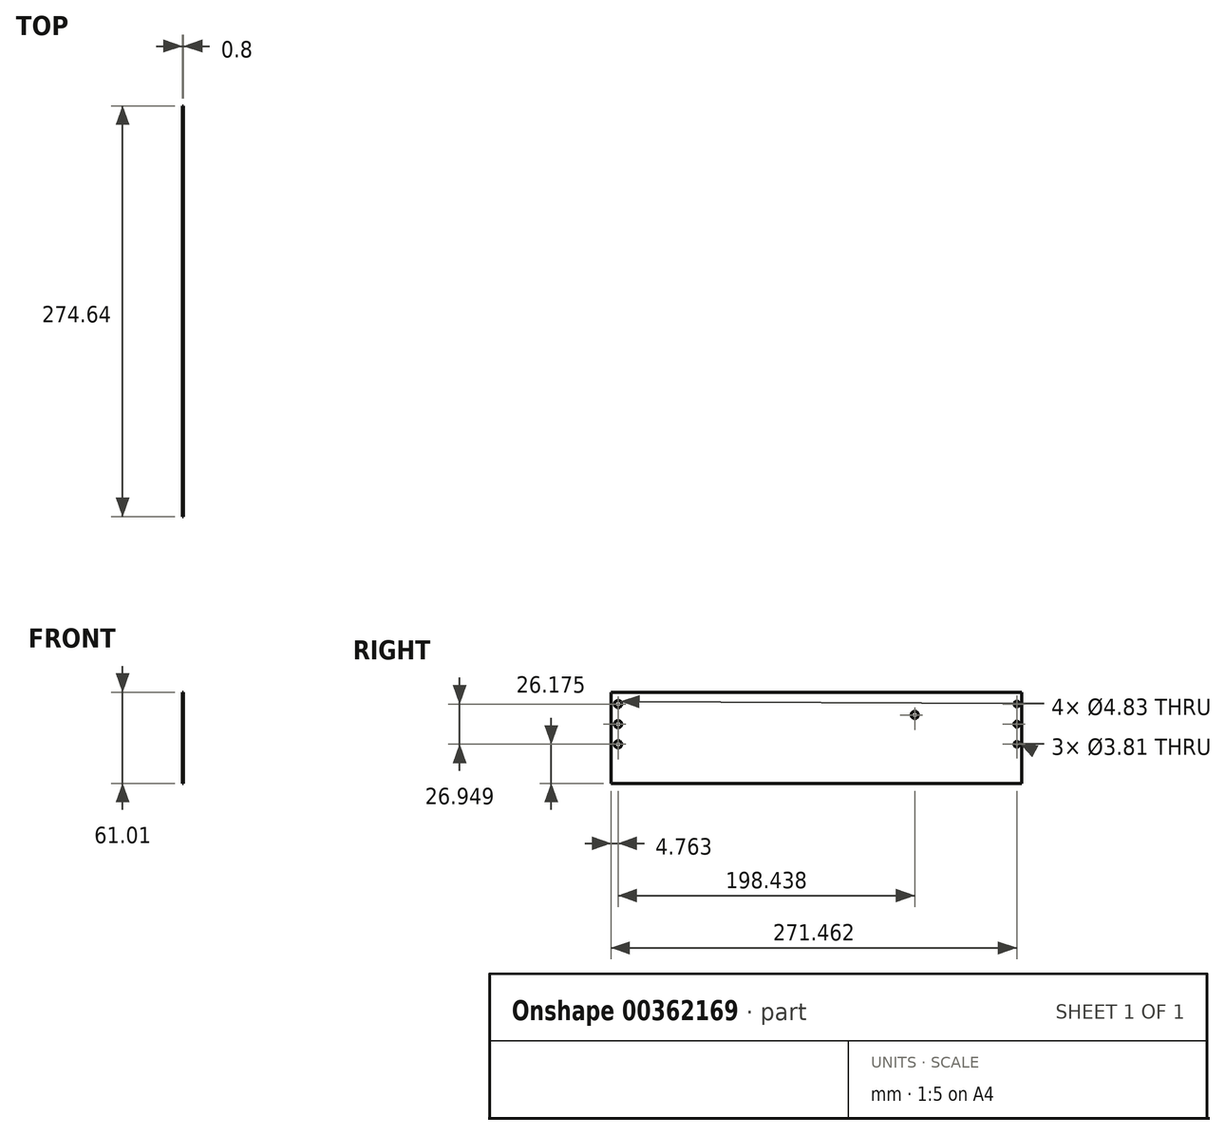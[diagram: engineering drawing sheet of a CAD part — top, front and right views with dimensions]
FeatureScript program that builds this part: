
annotation { "Feature Type Name" : "Feature", "Feature Type Description" : "" }
export const myFeature = defineFeature(function(context is Context, id is Id, definition is map)
    precondition{}
    {
        {
            var Q0;
            Q0=qCreatedBy(makeId("Right.planeOp"),FACE);
            var sketch = newSketch(context, id + "F0", { "sketchPlane" : qUnion([Q0])});
            skLineSegment(sketch, "E0", {"start": v(274.64, 0) * mm, "end": v(274.64, 53.9) * mm});
            skLineSegment(sketch, "E1", {"start": v(274.64, 53.9) * mm, "end": v(0, 53.9) * mm});
            skLineSegment(sketch, "E2", {"start": v(0, 53.9) * mm, "end": v(0, 0) * mm});
            skLineSegment(sketch, "E3", {"start": v(9.52, 53.9) * mm, "end": v(9.52, 0) * mm, "construction": true});
            skLineSegment(sketch, "E4", {"start": v(9.52, 26.95) * mm, "end": v(0, 26.95) * mm, "construction": true});
            skLineSegment(sketch, "E5", {"start": v(4.76, 0) * mm, "end": v(4.76, 26.95) * mm, "construction": true});
            skPoint(sketch, "E5.startSnap0", {"position": v(4.76, 26.95) * mm});
            skLineSegment(sketch, "E6", {"start": v(4.76, 26.95) * mm, "end": v(4.76, 53.9) * mm, "construction": true});
            skPoint(sketch, "E7", {"position": v(4.76, 40.42) * mm});
            skPoint(sketch, "E8", {"position": v(4.76, 13.47) * mm});
            skLineSegment(sketch, "E9", {"start": v(203.2, 53.9) * mm, "end": v(203.2, 0) * mm, "construction": true});
            skPoint(sketch, "E10", {"position": v(203.2, 33.14) * mm});
            skLineSegment(sketch, "E11", {"start": v(0, 0) * mm, "end": v(0, -12.7) * mm});
            skLineSegment(sketch, "E12", {"start": v(0, -12.7) * mm, "end": v(274.64, -12.7) * mm});
            skLineSegment(sketch, "E13", {"start": v(274.64, -12.7) * mm, "end": v(274.64, 0) * mm});
            skLineSegment(sketch, "E14", {"start": v(0, 0) * mm, "end": v(274.64, 0) * mm, "construction": true});
            skLineSegment(sketch, "E15", {"start": v(268.29, 53.9) * mm, "end": v(268.29, 0) * mm, "construction": true});
            skLineSegment(sketch, "E16", {"start": v(268.29, 26.95) * mm, "end": v(274.64, 26.95) * mm, "construction": true});
            skPoint(sketch, "E17.startSnap0", {"position": v(271.46, 26.95) * mm});
            skLineSegment(sketch, "E18", {"start": v(271.46, 0) * mm, "end": v(271.46, 26.95) * mm, "construction": true});
            skLineSegment(sketch, "E19", {"start": v(271.46, 53.9) * mm, "end": v(271.46, 26.95) * mm, "construction": true});
            skPoint(sketch, "E20", {"position": v(271.46, 40.42) * mm});
            skPoint(sketch, "E21", {"position": v(271.46, 13.47) * mm});
            skPoint(sketch, "E22", {"position": v(203.2, 25.59) * mm});
            skLineSegment(sketch, "E23", {"start": v(274.64, 48.31) * mm, "end": v(0, 48.31) * mm});
            skSolve(sketch);
        }
        {
            var Q0;
            {var subQ0=sQuery(id+"F0.wireOp",EDGE,"E11");Q0=makeQuery(id+"F0.imprint","IMPRINT",FACE,{"disambiguationData":[TD([[makeQuery(id+"F0.imprint","IMPRINT",EDGE,{"derivedFrom":subQ0}),1.0]])]});}
            extrude(context, id + "F1", {"entities" : qUnion([Q0]), "depth" : 0.8 * mm, "offsetDistance" : 25.4 * mm});
        }
        {
            var Q0;
            Q0=sQuery(id+"F0.wireOp",VERTEX,"E7");
            var Q1;
            Q1=sQuery(id+"F0.wireOp",VERTEX,"E5.startSnap0");
            var Q2;
            Q2=sQuery(id+"F0.wireOp",VERTEX,"E8");
            var Q3;
            Q3=sQuery(id+"F0.wireOp",VERTEX,"E10");
            var Q4;
            Q4=makeQuery(id+"F1.opExtrude","SWEPT_BODY",BODY,{"disambiguationData":[OSD([sQuery(id+"F0.wireOp",EDGE,"LokPoCD6-FjNM-1Vt9-Nqnl-R2dUqbxLQ1ov"),sQuery(id+"F0.wireOp",EDGE,"E0"),sQuery(id+"F0.wireOp",EDGE,"E1"),sQuery(id+"F0.wireOp",EDGE,"E2")])]});
            hole(context, id + "F2", {"style" : HoleStyle.SIMPLE, "endStyle" : HoleEndStyle.THROUGH, "oppositeDirection" : true, "holeDiameter" : 4.83 * mm, "isTappedThrough" : true, "tappedDepth" : 12.7 * mm, "tapClearance" : 3, "startFromSketch" : true, "locations" : qUnion([Q0, Q1, Q2, Q3]), "scope" : qUnion([Q4])});
        }
        {
            var Q0;
            Q0=sQuery(id+"F0.wireOp",VERTEX,"E20");
            var Q1;
            Q1=sQuery(id+"F0.wireOp",VERTEX,"E17.startSnap0");
            var Q2;
            Q2=sQuery(id+"F0.wireOp",VERTEX,"E21");
            var Q3;
            Q3=makeQuery(id+"F1.opExtrude","SWEPT_BODY",BODY,{"disambiguationData":[OSD([sQuery(id+"F0.wireOp",EDGE,"E0"),sQuery(id+"F0.wireOp",EDGE,"E1"),sQuery(id+"F0.wireOp",EDGE,"E2"),sQuery(id+"F0.wireOp",EDGE,"E11"),sQuery(id+"F0.wireOp",EDGE,"E12"),sQuery(id+"F0.wireOp",EDGE,"E13")])]});
            hole(context, id + "F3", {"style" : HoleStyle.SIMPLE, "endStyle" : HoleEndStyle.THROUGH, "oppositeDirection" : true, "holeDiameter" : 3.8 * mm, "isTappedThrough" : true, "tappedDepth" : 12.7 * mm, "tapClearance" : 3, "startFromSketch" : true, "locations" : qUnion([Q0, Q1, Q2]), "scope" : qUnion([Q3])});
        }
    });
